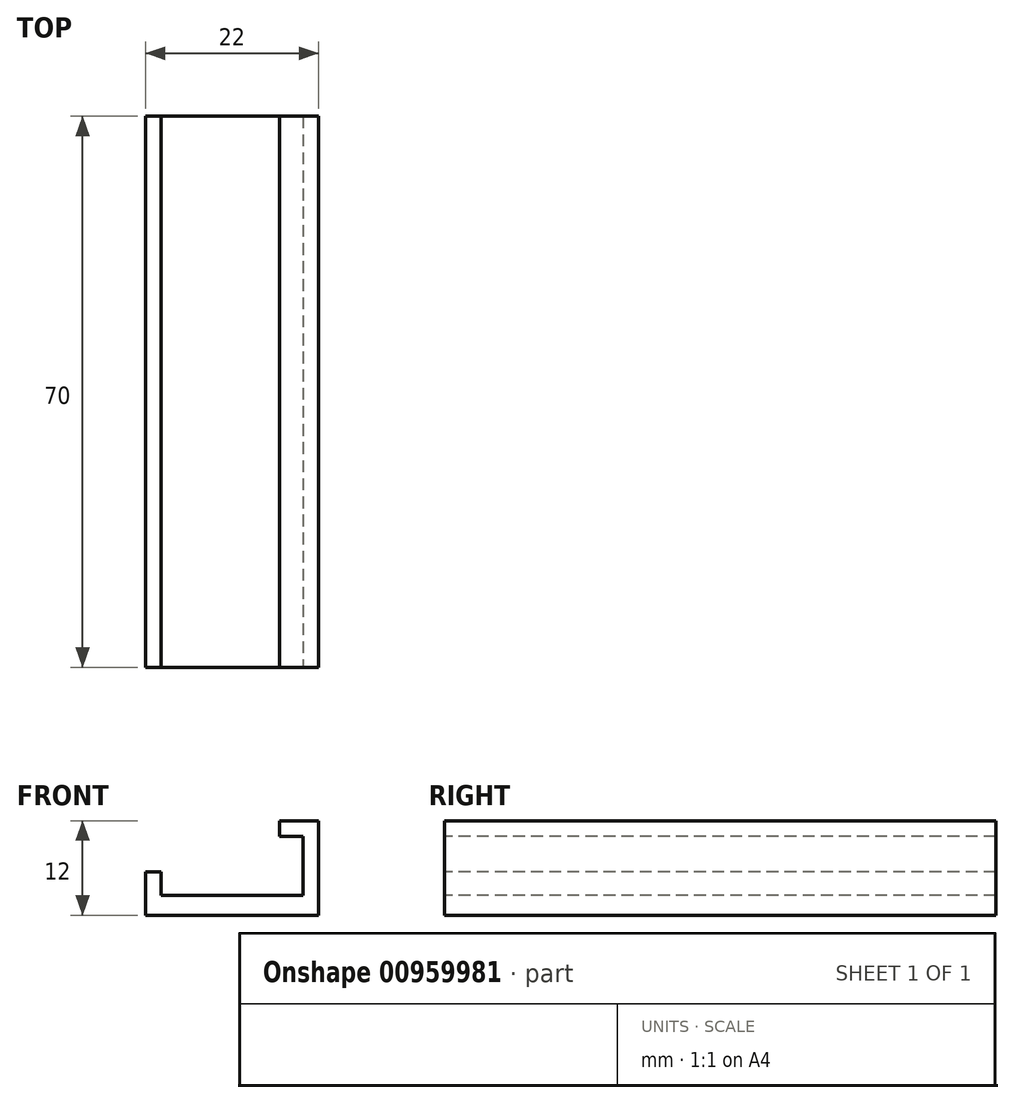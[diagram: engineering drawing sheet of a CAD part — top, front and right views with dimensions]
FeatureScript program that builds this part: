
annotation { "Feature Type Name" : "Feature", "Feature Type Description" : "" }
export const myFeature = defineFeature(function(context is Context, id is Id, definition is map)
    precondition{}
    {
        {
            var Q0;
            Q0=qCreatedBy(makeId("Top.planeOp"),FACE);
            var sketch = newSketch(context, id + "F0", { "sketchPlane" : qUnion([Q0])});
            skLineSegment(sketch, "E0.bottom", {"start": v(-14.22, 24.06) * mm, "end": v(7.78, 24.06) * mm});
            skLineSegment(sketch, "E0.top", {"start": v(-14.22, -45.94) * mm, "end": v(7.78, -45.94) * mm});
            skLineSegment(sketch, "E0.left", {"start": v(-14.22, 24.06) * mm, "end": v(-14.22, -45.94) * mm});
            skLineSegment(sketch, "E0.right", {"start": v(7.78, 24.06) * mm, "end": v(7.78, -45.94) * mm});
            skSolve(sketch);
        }
        {
            var Q0;
            Q0 = qSketchRegion(id + "F0", true);
            extrude(context, id + "F1", {"entities" : qUnion([Q0]), "depth" : 2.5 * mm, "offsetDistance" : 25 * mm});
        }
        {
            var Q0;
            Q0=makeQuery(id+"F1.opExtrude","CAP_FACE",FACE,{"disambiguationData":[OSD([sQuery(id+"F0.wireOp",EDGE,"E0.bottom"),sQuery(id+"F0.wireOp",EDGE,"E0.top"),sQuery(id+"F0.wireOp",EDGE,"E0.left"),sQuery(id+"F0.wireOp",EDGE,"E0.right")])],"isStart":false});
            var sketch = newSketch(context, id + "F2", { "sketchPlane" : qUnion([Q0])});
            skLineSegment(sketch, "E1.bottom", {"start": v(-14.22, 24.06) * mm, "end": v(-12.22, 24.06) * mm});
            skLineSegment(sketch, "E1.top", {"start": v(-14.22, -45.94) * mm, "end": v(-12.22, -45.94) * mm});
            skLineSegment(sketch, "E1.left", {"start": v(-14.22, 24.06) * mm, "end": v(-14.22, -45.94) * mm});
            skLineSegment(sketch, "E1.right", {"start": v(-12.22, 24.06) * mm, "end": v(-12.22, -45.94) * mm});
            skLineSegment(sketch, "E2.bottom", {"start": v(7.78, 24.06) * mm, "end": v(5.78, 24.06) * mm});
            skLineSegment(sketch, "E2.top", {"start": v(7.78, -45.94) * mm, "end": v(5.78, -45.94) * mm});
            skLineSegment(sketch, "E2.left", {"start": v(7.78, 24.06) * mm, "end": v(7.78, -45.94) * mm});
            skLineSegment(sketch, "E2.right", {"start": v(5.78, 24.06) * mm, "end": v(5.78, -45.94) * mm});
            skSolve(sketch);
        }
        {
            var Q0;
            Q0=makeQuery(id+"F2.imprint","IMPRINT",FACE,{"disambiguationData":[TD([[makeQuery(id+"F2.imprint","IMPRINT",EDGE,{"derivedFrom":sQuery(id+"F2.wireOp",EDGE,"E1.bottom")}),-1.0]])]});
            extrude(context, id + "F3", {"entities" : qUnion([Q0]), "operationType" : NewBodyOperationType.ADD, "depth" : 3 * mm, "offsetDistance" : 25 * mm});
        }
        {
            var Q0;
            Q0=makeQuery(id+"F2.imprint","IMPRINT",FACE,{"disambiguationData":[TD([[makeQuery(id+"F2.imprint","IMPRINT",EDGE,{"derivedFrom":sQuery(id+"F2.wireOp",EDGE,"E2.bottom")}),-1.0]])]});
            extrude(context, id + "F4", {"entities" : qUnion([Q0]), "operationType" : NewBodyOperationType.ADD, "depth" : 9.5 * mm, "offsetDistance" : 25 * mm});
        }
        {
            var Q0;
            Q0=makeQuery(id+"F4.opExtrude","SWEPT_FACE",FACE,{"disambiguationData":[OSD([sQuery(id+"F2.wireOp",EDGE,"E2.right")])]});
            var sketch = newSketch(context, id + "F5", { "sketchPlane" : qUnion([Q0])});
            skLineSegment(sketch, "E3.bottom", {"start": v(-24.06, 12) * mm, "end": v(45.94, 12) * mm});
            skLineSegment(sketch, "E3.top", {"start": v(-24.06, 10) * mm, "end": v(45.94, 10) * mm});
            skLineSegment(sketch, "E3.left", {"start": v(-24.06, 12) * mm, "end": v(-24.06, 10) * mm});
            skLineSegment(sketch, "E3.right", {"start": v(45.94, 12) * mm, "end": v(45.94, 10) * mm});
            skSolve(sketch);
        }
        {
            var Q0;
            Q0=makeQuery(id+"F5.imprint","IMPRINT",FACE,{"disambiguationData":[TD([[makeQuery(id+"F5.imprint","IMPRINT",EDGE,{"derivedFrom":sQuery(id+"F5.wireOp",EDGE,"E3.bottom")}),-1.0]])]});
            extrude(context, id + "F6", {"entities" : qUnion([Q0]), "operationType" : NewBodyOperationType.ADD, "depth" : 3 * mm, "offsetDistance" : 25 * mm});
        }
    });
